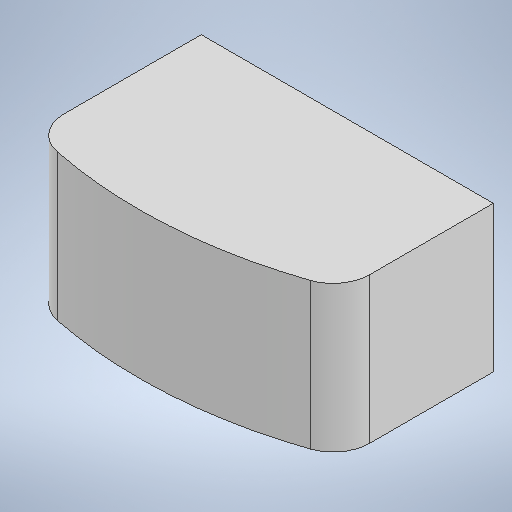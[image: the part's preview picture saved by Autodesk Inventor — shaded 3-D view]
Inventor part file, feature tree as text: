
AUTODESK INVENTOR PART (.ipt)
format: ipt  version: 2025 (Build 290162000, 162)  size: 263,680 bytes
history: native  units: in
note: dims shown in document units (in); Inventor stores cm internally (conversion verified against a paired STEP export)
features: other x1, extrude x1, fillet x1, sketch x1
ambient origin geometry x8: Origin, YZ Plane, XZ Plane, XY Plane, X Axis, Y Axis, Z Axis, Center Point
bodies: Body1 (feature_tree)
feature tree (4):
  other  "ソリッド1"
  extrude  "押し出し1"  Depth=3.1496in
  fillet  "フィレット1"  Radius=1.9685in
  sketch  "スケッチ1"
